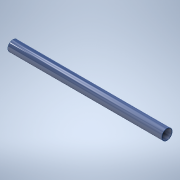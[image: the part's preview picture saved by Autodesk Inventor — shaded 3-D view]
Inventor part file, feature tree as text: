
AUTODESK INVENTOR PART (.ipt)
format: ipt  version: 2020 (Build 240168000, 168)  size: 115,200 bytes
history: native  units: mm
features: revolve x1, sketch x1
ambient origin geometry x8: Origin, YZ Plane, XZ Plane, XY Plane, X Axis, Y Axis, Z Axis, Center Point
bodies: Solid1 (feature_tree)
feature tree (2):
  revolve  "Revolution1"  [1 undecoded]
  sketch  "Sketch1"  dims[d0=1150.0mm d1=39.5mm d2=2.0mm d3=90.0deg]
note: 1 required parameter value undecoded (feature->parameter linkage not recoverable at this tier; creation-order binding heuristic only, values carry confidence <= 0.55)
